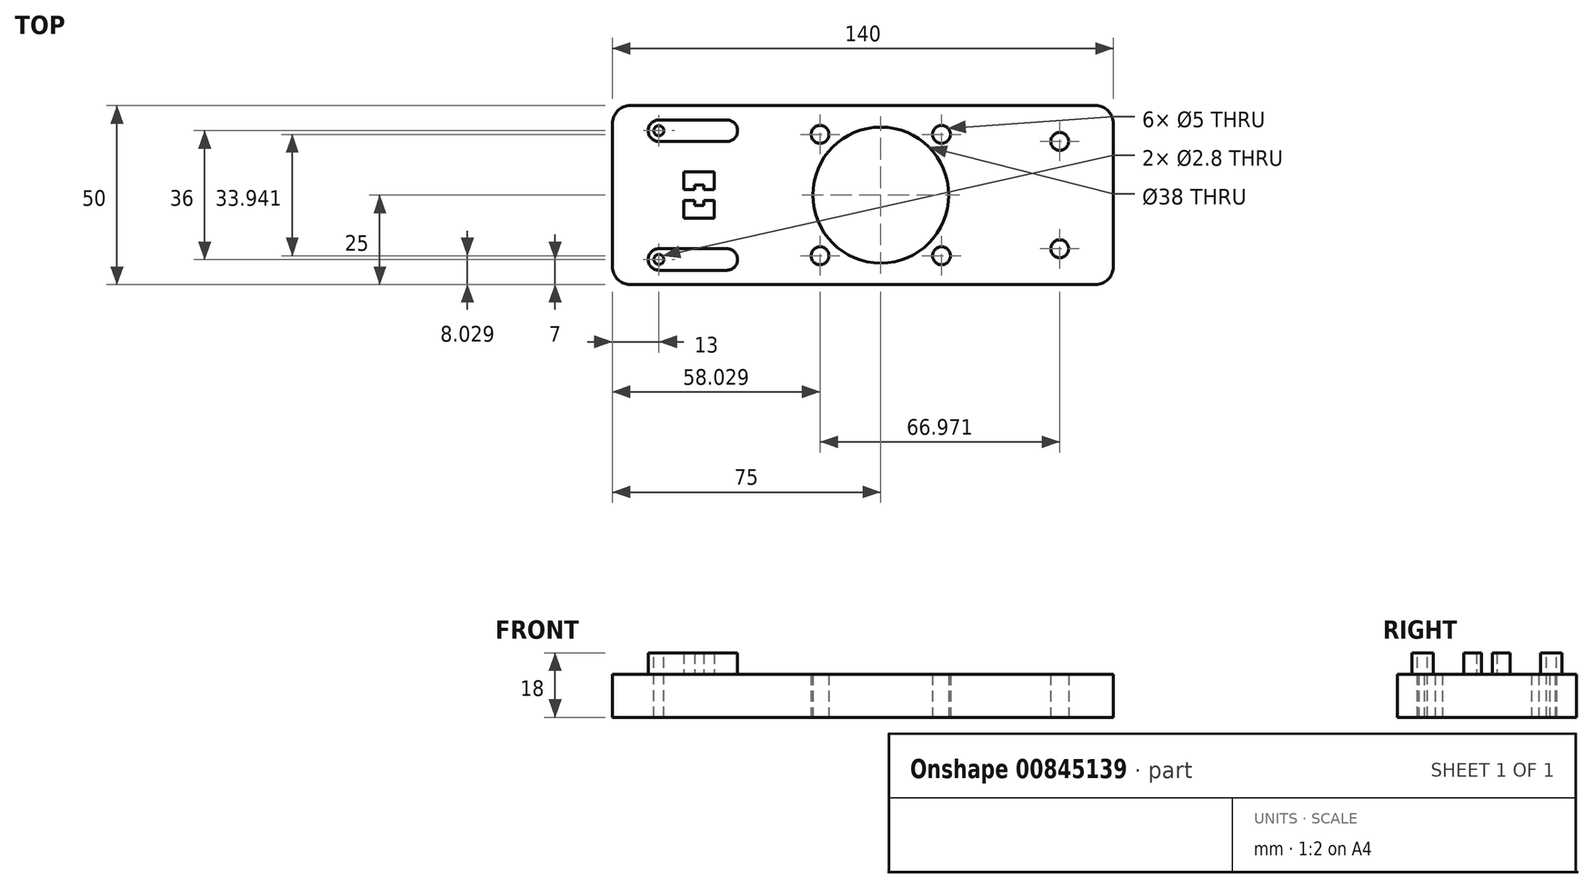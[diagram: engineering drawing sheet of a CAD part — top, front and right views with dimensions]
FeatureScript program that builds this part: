
annotation { "Feature Type Name" : "Feature", "Feature Type Description" : "" }
export const myFeature = defineFeature(function(context is Context, id is Id, definition is map)
    precondition{}
    {
        {
            var Q0;
            Q0=qCreatedBy(makeId("Top.planeOp"),FACE);
            var sketch = newSketch(context, id + "F0", { "sketchPlane" : qUnion([Q0])});
            skLineSegment(sketch, "E0.bottom", {"start": v(25, 25) * mm, "end": v(-25, 25) * mm});
            skLineSegment(sketch, "E0.top", {"start": v(25, -25) * mm, "end": v(-25, -25) * mm});
            skLineSegment(sketch, "E0.left", {"start": v(25, 25) * mm, "end": v(25, -25) * mm});
            skLineSegment(sketch, "E0.right", {"start": v(-25, 25) * mm, "end": v(-25, -25) * mm});
            skPoint(sketch, "E0.middle", {"position": v(0, 0) * mm});
            skCircle(sketch, "E1", {"center": v(0, 0) * mm, "radius": 24 * mm, "construction": true});
            skLineSegment(sketch, "E2.bottom", {"start": v(21, -21) * mm, "end": v(-21, -21) * mm, "construction": true});
            skLineSegment(sketch, "E2.top", {"start": v(21, 21) * mm, "end": v(-21, 21) * mm, "construction": true});
            skLineSegment(sketch, "E2.left", {"start": v(21, -21) * mm, "end": v(21, 21) * mm, "construction": true});
            skLineSegment(sketch, "E2.right", {"start": v(-21, -21) * mm, "end": v(-21, 21) * mm, "construction": true});
            skLineSegment(sketch, "E3", {"start": v(-21, 21) * mm, "end": v(25, -25) * mm, "construction": true});
            skLineSegment(sketch, "E4", {"start": v(21, 21) * mm, "end": v(-25, -25) * mm, "construction": true});
            skCircle(sketch, "E5", {"center": v(-16.97, 16.97) * mm, "radius": 2.5 * mm});
            skCircle(sketch, "E6", {"center": v(16.97, 16.97) * mm, "radius": 2.5 * mm});
            skCircle(sketch, "E7", {"center": v(16.97, -16.97) * mm, "radius": 2.5 * mm});
            skCircle(sketch, "E8", {"center": v(-16.97, -16.97) * mm, "radius": 2.5 * mm});
            skCircle(sketch, "E9", {"center": v(0, 0) * mm, "radius": 19 * mm});
            skCircle(sketch, "E10", {"center": v(0, 0) * mm, "radius": 15 * mm, "construction": true});
            skLineSegment(sketch, "E11.bottom", {"start": v(25, -25) * mm, "end": v(65, -25) * mm});
            skLineSegment(sketch, "E11.top", {"start": v(25, 25) * mm, "end": v(65, 25) * mm});
            skLineSegment(sketch, "E11.left", {"start": v(25, -25) * mm, "end": v(25, 25) * mm});
            skLineSegment(sketch, "E11.right", {"start": v(65, -25) * mm, "end": v(65, 25) * mm});
            skLineSegment(sketch, "E12", {"start": v(50, 25) * mm, "end": v(50, -25) * mm, "construction": true});
            skLineSegment(sketch, "E13", {"start": v(25, -15) * mm, "end": v(65, -15) * mm, "construction": true});
            skLineSegment(sketch, "E14", {"start": v(25, 15) * mm, "end": v(65, 15) * mm, "construction": true});
            skCircle(sketch, "E15", {"center": v(50, 15) * mm, "radius": 2.5 * mm});
            skCircle(sketch, "E16", {"center": v(50, -15) * mm, "radius": 2.5 * mm});
            skLineSegment(sketch, "E17.bottom", {"start": v(-25, -25) * mm, "end": v(-75, -25) * mm});
            skLineSegment(sketch, "E17.top", {"start": v(-25, 25) * mm, "end": v(-75, 25) * mm});
            skLineSegment(sketch, "E17.left", {"start": v(-25, -25) * mm, "end": v(-25, 25) * mm});
            skLineSegment(sketch, "E17.right", {"start": v(-75, -25) * mm, "end": v(-75, 25) * mm});
            skSolve(sketch);
        }
        {
            var Q0;
            Q0=qSketchRegion(id+"F0",true);
            extrude(context, id + "F1", {"entities" : qUnion([Q0]), "depth" : 12 * mm, "offsetDistance" : 25 * mm});
        }
        {
            var Q0;
            Q0=makeQuery(id+"F1.opExtrude","SWEPT_EDGE",EDGE,{"disambiguationData":[OSD([sQuery(id+"F0.wireOp",EDGE,"E11.bottom"),sQuery(id+"F0.wireOp",EDGE,"E11.right")])]});
            var Q1;
            Q1=makeQuery(id+"F1.opExtrude","SWEPT_EDGE",EDGE,{"disambiguationData":[OSD([sQuery(id+"F0.wireOp",EDGE,"E0.top"),sQuery(id+"F0.wireOp",EDGE,"E0.right")])]});
            var Q2;
            Q2=makeQuery(id+"F1.opExtrude","SWEPT_EDGE",EDGE,{"disambiguationData":[OSD([sQuery(id+"F0.wireOp",EDGE,"E0.bottom"),sQuery(id+"F0.wireOp",EDGE,"E0.right")])]});
            var Q3;
            Q3=makeQuery(id+"F1.opExtrude","SWEPT_EDGE",EDGE,{"disambiguationData":[OSD([sQuery(id+"F0.wireOp",EDGE,"E11.top"),sQuery(id+"F0.wireOp",EDGE,"E11.right")])]});
            var Q4;
            Q4=makeQuery(id+"F1.opExtrude","SWEPT_EDGE",EDGE,{"disambiguationData":[OSD([sQuery(id+"F0.wireOp",EDGE,"E17.bottom"),sQuery(id+"F0.wireOp",EDGE,"E17.right")])]});
            var Q5;
            Q5=makeQuery(id+"F1.opExtrude","SWEPT_EDGE",EDGE,{"disambiguationData":[OSD([sQuery(id+"F0.wireOp",EDGE,"E17.top"),sQuery(id+"F0.wireOp",EDGE,"E17.right")])]});
            fillet(context, id + "F2", {"entities" : qUnion([Q0, Q1, Q2, Q3, Q4, Q5]), "radius" : 5 * mm, "tangentPropagation" : true, "allowEdgeOverflow" : false});
        }
        {
            var Q0;
            Q0=makeQuery(id+"F1.opExtrude","CAP_FACE",FACE,{"disambiguationData":[OSD([sQuery(id+"F0.wireOp",EDGE,"E0.bottom"),sQuery(id+"F0.wireOp",EDGE,"E0.top"),sQuery(id+"F0.wireOp",EDGE,"E5"),sQuery(id+"F0.wireOp",EDGE,"E6"),sQuery(id+"F0.wireOp",EDGE,"E7"),sQuery(id+"F0.wireOp",EDGE,"E8"),sQuery(id+"F0.wireOp",EDGE,"E9"),sQuery(id+"F0.wireOp",EDGE,"E11.bottom"),sQuery(id+"F0.wireOp",EDGE,"E11.top"),sQuery(id+"F0.wireOp",EDGE,"E11.right"),sQuery(id+"F0.wireOp",EDGE,"E15"),sQuery(id+"F0.wireOp",EDGE,"E16"),sQuery(id+"F0.wireOp",EDGE,"E17.bottom"),sQuery(id+"F0.wireOp",EDGE,"E17.top"),sQuery(id+"F0.wireOp",EDGE,"E17.right")])],"isStart":false});
            var sketch = newSketch(context, id + "F3", { "sketchPlane" : qUnion([Q0])});
            skLineSegment(sketch, "E18.bottom", {"start": v(-55, 21) * mm, "end": v(-40, 21) * mm});
            skLineSegment(sketch, "E18.top", {"start": v(-55, 15) * mm, "end": v(-40, 15) * mm});
            skLineSegment(sketch, "E18.left", {"start": v(-55, 21) * mm, "end": v(-55, 15) * mm});
            skLineSegment(sketch, "E18.right", {"start": v(-40, 21) * mm, "end": v(-40, 15) * mm});
            skLineSegment(sketch, "E19.bottom", {"start": v(-55, -15) * mm, "end": v(-40, -15) * mm});
            skLineSegment(sketch, "E19.top", {"start": v(-55, -21) * mm, "end": v(-40, -21) * mm});
            skLineSegment(sketch, "E19.left", {"start": v(-55, -15) * mm, "end": v(-55, -21) * mm});
            skLineSegment(sketch, "E19.right", {"start": v(-40, -15) * mm, "end": v(-40, -21) * mm});
            skLineSegment(sketch, "E20.bottom", {"start": v(-55, 6.5) * mm, "end": v(-46.5, 6.5) * mm});
            skLineSegment(sketch, "E20.left", {"start": v(-55, 6.5) * mm, "end": v(-55, 1.5) * mm});
            skLineSegment(sketch, "E21.top", {"start": v(-49.5, 1.5) * mm, "end": v(-46.5, 1.5) * mm});
            skLineSegment(sketch, "E22.top", {"start": v(-46.5, -1.5) * mm, "end": v(-49.5, -1.5) * mm});
            skLineSegment(sketch, "E22.left", {"start": v(-46.5, -6.5) * mm, "end": v(-46.5, -1.5) * mm});
            skLineSegment(sketch, "E23.bottom", {"start": v(-46.5, -6.5) * mm, "end": v(-55, -6.5) * mm});
            skLineSegment(sketch, "E23.top", {"start": v(-52, -1.5) * mm, "end": v(-55, -1.5) * mm});
            skLineSegment(sketch, "E23.right", {"start": v(-55, -6.5) * mm, "end": v(-55, -1.5) * mm});
            skLineSegment(sketch, "E24", {"start": v(-46.5, 1.5) * mm, "end": v(-46.5, 6.5) * mm});
            skLineSegment(sketch, "E25", {"start": v(-55, 1.5) * mm, "end": v(-52, 1.5) * mm});
            skLineSegment(sketch, "E26", {"start": v(-52, 1.5) * mm, "end": v(-52, 2.85) * mm});
            skLineSegment(sketch, "E27", {"start": v(-49.5, 1.5) * mm, "end": v(-49.5, 2.85) * mm});
            skLineSegment(sketch, "E28", {"start": v(-52, -1.5) * mm, "end": v(-52, -2.85) * mm});
            skLineSegment(sketch, "E29", {"start": v(-49.5, -1.5) * mm, "end": v(-49.5, -2.85) * mm});
            skLineSegment(sketch, "E30", {"start": v(-49.5, -2.85) * mm, "end": v(-52, -2.85) * mm});
            skLineSegment(sketch, "E31", {"start": v(-49.5, 2.85) * mm, "end": v(-52, 2.85) * mm});
            skLineSegment(sketch, "E32.bottom", {"start": v(-55, 21) * mm, "end": v(-65, 21) * mm});
            skLineSegment(sketch, "E32.top", {"start": v(-55, 15) * mm, "end": v(-65, 15) * mm});
            skLineSegment(sketch, "E32.right", {"start": v(-65, 21) * mm, "end": v(-65, 15) * mm});
            skLineSegment(sketch, "E33.bottom", {"start": v(-55, -15) * mm, "end": v(-65, -15) * mm});
            skLineSegment(sketch, "E33.top", {"start": v(-55, -21) * mm, "end": v(-65, -21) * mm});
            skLineSegment(sketch, "E33.right", {"start": v(-65, -15) * mm, "end": v(-65, -21) * mm});
            skSolve(sketch);
        }
        {
            var Q0;
            Q0 = qSketchRegion(id + "F3", true);
            extrude(context, id + "F4", {"entities" : qUnion([Q0]), "operationType" : NewBodyOperationType.ADD, "depth" : 6 * mm, "offsetDistance" : 25 * mm});
        }
        {
            var Q0;
            Q0=makeQuery(id+"F4.opExtrude","SWEPT_EDGE",EDGE,{"disambiguationData":[OSD([sQuery(id+"F3.wireOp",EDGE,"E32.bottom"),sQuery(id+"F3.wireOp",EDGE,"E32.right")])]});
            var Q1;
            Q1=makeQuery(id+"F4.opExtrude","SWEPT_EDGE",EDGE,{"disambiguationData":[OSD([sQuery(id+"F3.wireOp",EDGE,"E32.top"),sQuery(id+"F3.wireOp",EDGE,"E32.right")])]});
            var Q2;
            Q2=makeQuery(id+"F4.opExtrude","SWEPT_EDGE",EDGE,{"disambiguationData":[OSD([sQuery(id+"F3.wireOp",EDGE,"E18.top"),sQuery(id+"F3.wireOp",EDGE,"E18.right")])]});
            var Q3;
            Q3=makeQuery(id+"F4.opExtrude","SWEPT_EDGE",EDGE,{"disambiguationData":[OSD([sQuery(id+"F3.wireOp",EDGE,"E33.bottom"),sQuery(id+"F3.wireOp",EDGE,"E33.right")])]});
            var Q4;
            Q4=makeQuery(id+"F4.opExtrude","SWEPT_EDGE",EDGE,{"disambiguationData":[OSD([sQuery(id+"F3.wireOp",EDGE,"E33.top"),sQuery(id+"F3.wireOp",EDGE,"E33.right")])]});
            var Q5;
            Q5=makeQuery(id+"F4.opExtrude","SWEPT_EDGE",EDGE,{"disambiguationData":[OSD([sQuery(id+"F3.wireOp",EDGE,"E19.top"),sQuery(id+"F3.wireOp",EDGE,"E19.right")])]});
            var Q6;
            Q6=makeQuery(id+"F4.opExtrude","SWEPT_EDGE",EDGE,{"disambiguationData":[OSD([sQuery(id+"F3.wireOp",EDGE,"E19.bottom"),sQuery(id+"F3.wireOp",EDGE,"E19.right")])]});
            var Q7;
            Q7=makeQuery(id+"F4.opExtrude","SWEPT_EDGE",EDGE,{"disambiguationData":[OSD([sQuery(id+"F3.wireOp",EDGE,"E18.bottom"),sQuery(id+"F3.wireOp",EDGE,"E18.right")])]});
            fillet(context, id + "F5", {"entities" : qUnion([Q0, Q1, Q2, Q3, Q4, Q5, Q6, Q7]), "radius" : 3 * mm, "tangentPropagation" : true, "allowEdgeOverflow" : false});
        }
        {
            var Q0;
            Q0=makeQuery(id+"F4.opExtrude","CAP_FACE",FACE,{"disambiguationData":[OSD([sQuery(id+"F3.wireOp",EDGE,"E18.bottom"),sQuery(id+"F3.wireOp",EDGE,"E18.top"),sQuery(id+"F3.wireOp",EDGE,"E18.right"),sQuery(id+"F3.wireOp",EDGE,"E32.bottom"),sQuery(id+"F3.wireOp",EDGE,"E32.top"),sQuery(id+"F3.wireOp",EDGE,"E32.right")])],"isStart":false});
            var sketch = newSketch(context, id + "F6", { "sketchPlane" : qUnion([Q0])});
            skCircle(sketch, "E34", {"center": v(-62, 18) * mm, "radius": 1.4 * mm});
            skCircle(sketch, "E35", {"center": v(-62, -18) * mm, "radius": 1.4 * mm});
            skSolve(sketch);
        }
        {
            var Q0;
            Q0 = qSketchRegion(id + "F6", true);
            extrude(context, id + "F7", {"entities" : qUnion([Q0]), "operationType" : NewBodyOperationType.REMOVE, "endBound" : BoundingType.UP_TO_NEXT, "oppositeDirection" : true, "depth" : 25 * mm, "offsetDistance" : 25 * mm});
        }
    });
